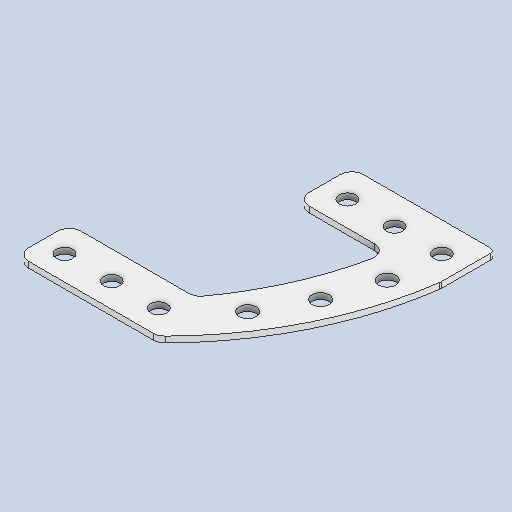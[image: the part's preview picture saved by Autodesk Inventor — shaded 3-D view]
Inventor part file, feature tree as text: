
AUTODESK INVENTOR PART (.ipt)
format: ipt  version: 2025.2 (Build 292293000, 293)  size: 136,704 bytes
history: native  units: in
note: dims shown in document units (in); Inventor stores cm internally (conversion verified against a paired STEP export)
features: extrude x1, sketch x1
ambient origin geometry x8: Origin, YZ Plane, XZ Plane, XY Plane, X Axis, Y Axis, Z Axis, Center Point
bodies: Solid1 (feature_tree)
feature tree (2):
  extrude  "Extrusion1"  Depth=0.0625in TaperAngle=0.0deg
  sketch  "Sketch1"  dims[d0=0.125in d1=0.125in d2=0.05in d3=0.182in d4=0.182in d5=0.182in d6=0.0625in d7=0.0in]
